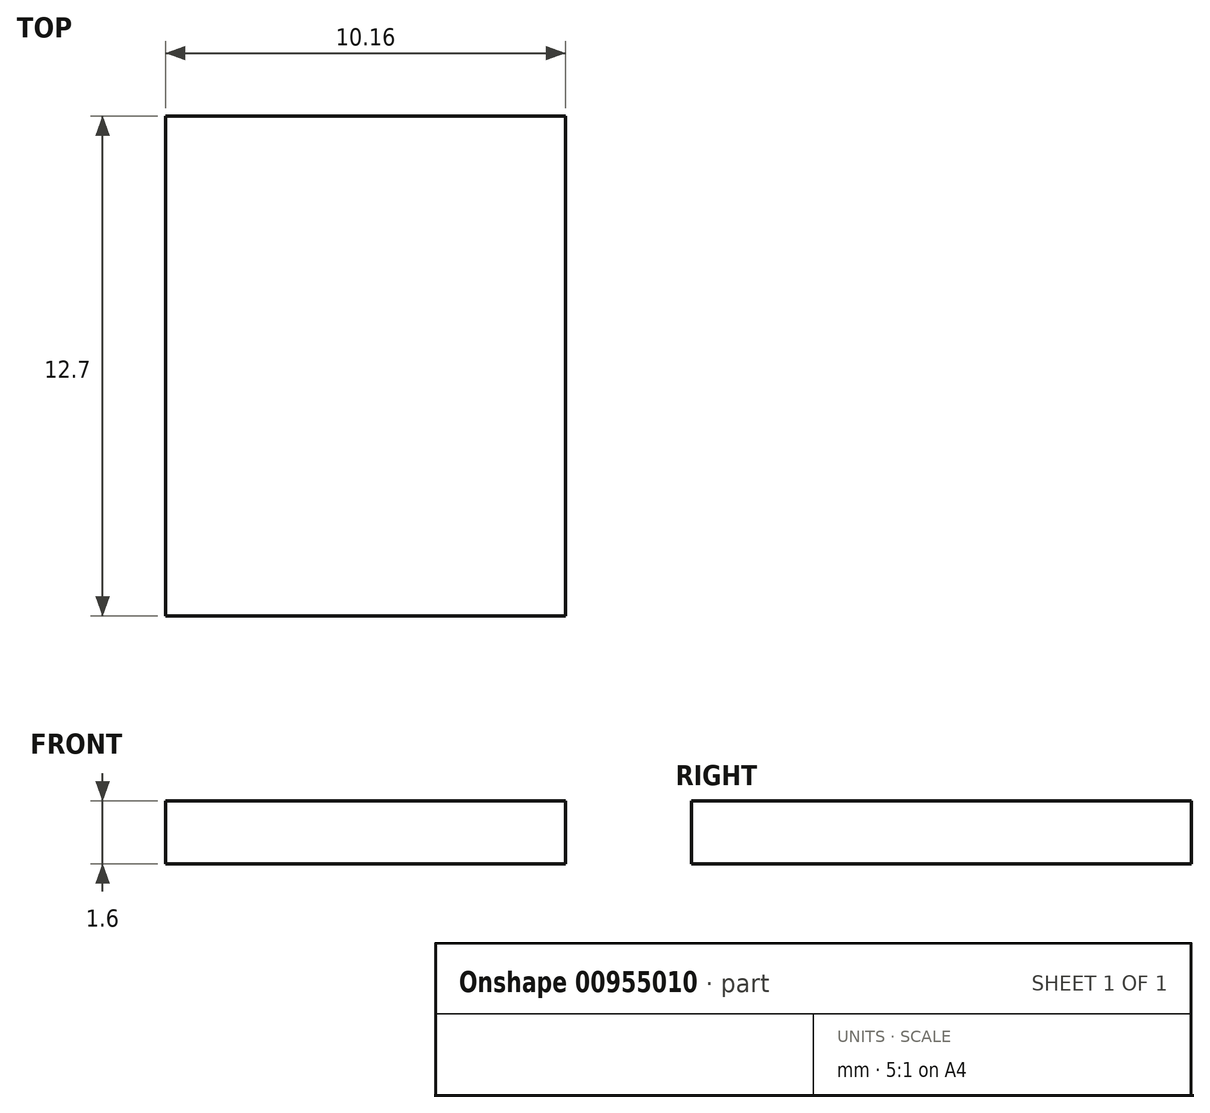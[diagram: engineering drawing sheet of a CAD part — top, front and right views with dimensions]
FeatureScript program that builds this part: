
annotation { "Feature Type Name" : "Feature", "Feature Type Description" : "" }
export const myFeature = defineFeature(function(context is Context, id is Id, definition is map)
    precondition{}
    {
        {
            var Q0;
            Q0=qCreatedBy(makeId("Top.planeOp"),FACE);
            var sketch = newSketch(context, id + "F0", { "sketchPlane" : qUnion([Q0])});
            skLineSegment(sketch, "E0.bottom", {"start": v(0, 0) * mm, "end": v(10.16, 0) * mm});
            skLineSegment(sketch, "E0.top", {"start": v(0, 12.7) * mm, "end": v(10.16, 12.7) * mm});
            skLineSegment(sketch, "E0.left", {"start": v(0, 0) * mm, "end": v(0, 12.7) * mm});
            skLineSegment(sketch, "E0.right", {"start": v(10.16, 0) * mm, "end": v(10.16, 12.7) * mm});
            skSolve(sketch);
        }
        {
            var Q0;
            Q0 = qSketchRegion(id + "F0", true);
            extrude(context, id + "F1", {"entities" : qUnion([Q0]), "depth" : 1.6 * mm, "offsetDistance" : 25.4 * mm});
        }
    });
